# Revit family: DF_МуфтаСоеденительная_Болтовая_EZETEK
name_source: partatom
category: Соединительные детали воздуховодов
revit_build: Autodesk Revit 2017 (Build: 20170118_1100(x64)
units: mm (PartAtom-declared; Revit-internal decimal feet)

## family parameters
Всегда вертикально = Да
На основе рабочей плоскости = Нет
Общий = Нет
При загрузке вырезать с полостями = Нет
Размер круглого соединителя = Использовать радиус
Тип детали = Соединение

## types (2) — shared parameters
ADSK_Версия Revit = 2017
ADSK_Единица измерения = Неспецифицируемое
ADSK_Завод-изготовитель = Неспецифицируемое
ADSK_Код изделия = Неспецифицируемое
ADSK_Марка = Неспецифицируемое
ADSK_Масса_Текст = Неспецифицируемое
ADSK_Наименование = Неспецифицируемое
ADSK_Обозначение = Неспецифицируемое
URL = https://ezetek.ru
Группа модели = Молниеприемники и комплектующие к вертикальным поверхностям
Изготовитель = Ezetek
zero-valued in all types: ADSK_Количество, ADSK_Масса

## per-type parameters (varying)
| type | ADSK_Материал | Code | Тип |
| МуфтаСоединительная_10-16_74624 | BIMLIB_Сталь_Нержавеющая_EZETEK | 2 мм | FA_МуфтаСоеденительная_Болтовая_EZETEK : МуфтаСоединительная_10-16 мм_74624 |
| МуфтаСоединительная_8-10_74634 | BIMLIB_Алюминий_EZETEK | 1 мм | FA_МуфтаСоеденительная_Болтовая_EZETEK : МуфтаСоединительная_8-10 мм_74634 |
